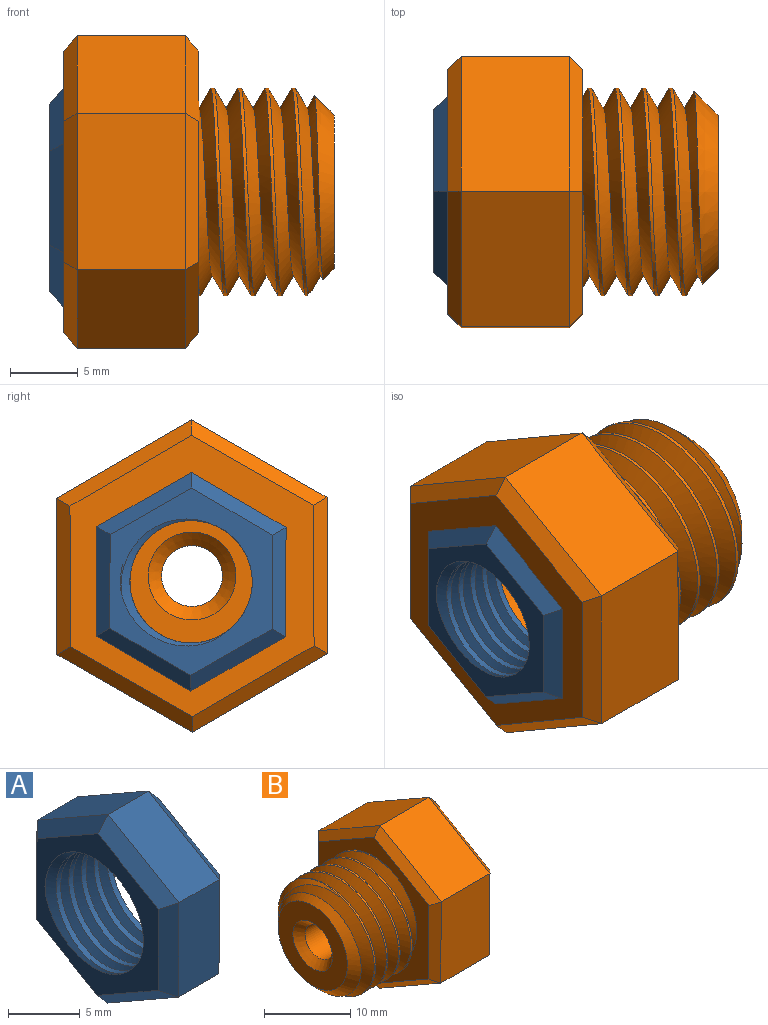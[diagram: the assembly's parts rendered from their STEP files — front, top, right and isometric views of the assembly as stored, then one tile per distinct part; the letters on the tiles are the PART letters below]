
ASSEMBLY  parts=2 mates=1
PART A: 23 faces, bbox 7.5x14.4x16.6 mm
  f0: cylinder r=4.52mm len=9.05mm, axis (1,0,0), area 59.9mm2, adj f7,f8,f21,f22
  f1: plane 6.98x4.07mm, normal (0,-0.5,0.86), area 32.3mm2, adj f2,f6,f14,f18
  f2: plane 8.08x4mm, normal (0,-1,0), area 32.3mm2, adj f1,f3,f12,f16
  f3: plane 7.02x4.01mm, normal (0,-0.5,-0.87), area 32.3mm2, adj f2,f4,f10,f15
  f4: plane 6.98x4.07mm, normal (0,0.5,-0.86), area 32.3mm2, adj f3,f5,f9,f17
  f5: plane 8.08x4mm, normal (0,1,0), area 32.3mm2, adj f4,f6,f11,f19
  f6: plane 7.02x4.01mm, normal (0,0.5,0.87), area 32.3mm2, adj f1,f5,f13,f20
  f7: plane 14.25x12.43mm, normal (-1,0,0), area 53.6mm2, adj f0,f9,f10,f11,f12,f13,f14,f21
  f8: plane 14.27x12.44mm, normal (1,0,0), area 53.6mm2, adj f0,f15,f16,f17,f18,f19,f20,f21
  f9: plane 6.99x4.65mm, normal (-0.71,0.36,-0.61), area 10.6mm2, adj f4,f7,f10,f11
  f10: plane 7.02x4.59mm, normal (-0.71,-0.35,-0.61), area 10.6mm2, adj f3,f7,f9,f12
  f11: plane 8.08x1.03mm, normal (-0.71,0.71,0), area 10.6mm2, adj f5,f7,f9,f13
  f12: plane 8.08x1.03mm, normal (-0.71,-0.71,0), area 10.6mm2, adj f2,f7,f10,f14
  f13: plane 7.02x4.59mm, normal (-0.71,0.35,0.61), area 10.6mm2, adj f6,f7,f11,f14
  f14: plane 6.99x4.65mm, normal (-0.71,-0.36,0.61), area 10.6mm2, adj f1,f7,f12,f13
  f15: plane 7.02x4.59mm, normal (0.71,-0.35,-0.61), area 10.6mm2, adj f3,f8,f16,f17
  f16: plane 8.08x1.03mm, normal (0.71,-0.71,0), area 10.6mm2, adj f2,f8,f15,f18
  f17: plane 6.99x4.65mm, normal (0.71,0.36,-0.61), area 10.6mm2, adj f4,f8,f15,f19
  f18: plane 6.99x4.65mm, normal (0.71,-0.36,0.61), area 10.6mm2, adj f1,f8,f16,f20
  f19: plane 8.08x1.03mm, normal (0.71,0.71,0), area 10.6mm2, adj f5,f8,f17,f20
  f20: plane 7.02x4.59mm, normal (0.71,0.35,0.61), area 10.6mm2, adj f6,f8,f18,f19
  f21: bspline ~12.07x10.45mm, area 119.5mm2, adj f0,f7,f8,f22
  f22: bspline ~12.07x10.45mm, area 119.6mm2, adj f0,f7,f8,f21
PART B: 30 faces, bbox 21.7x21.2x24.2 mm
  f0: cylinder r=7.68mm len=15.36mm, axis (1,0,0), area 50.1mm2, adj f1,f2,f4,f12
  f1: bspline ~17.74x15.36mm, area 332.4mm2, adj f0,f2,f4,f12
  f2: bspline ~17.74x15.36mm, area 332.4mm2, adj f0,f1,f4,f12
  f3: plane 11.36x11.36mm, normal (-1,0,0), area 68.2mm2, adj f4,f28
  f4: cone r=7.68mm half-angle=45deg, axis (1,0,0), area 76.5mm2, adj f0,f1,f2,f3
  f5: plane 9.98x8mm, normal (0,-0.5,0.86), area 92.4mm2, adj f6,f10,f18,f22
  f6: plane 11.55x8mm, normal (0,-1,0), area 92.4mm2, adj f5,f7,f16,f20
  f7: plane 10.02x8mm, normal (0,-0.5,-0.87), area 92.4mm2, adj f6,f8,f14,f19
  f8: plane 9.98x8mm, normal (0,0.5,-0.86), area 92.4mm2, adj f7,f9,f13,f21
  f9: plane 11.55x8mm, normal (0,1,0), area 92.4mm2, adj f8,f10,f15,f23
  f10: plane 10.02x8mm, normal (0,0.5,0.87), area 92.4mm2, adj f5,f9,f17,f24
  f11: plane 20.78x18.04mm, normal (1,0,0), area 167.5mm2, adj f13,f14,f15,f16,f17,f18,f25
  f12: plane 21.9x19.16mm, normal (-1,0,0), area 125.2mm2, adj f0,f1,f2,f19,f20,f21,f22,f23
  f13: plane 9.98x6.38mm, normal (0.71,0.36,-0.61), area 15.5mm2, adj f8,f11,f14,f15
  f14: plane 10.02x6.32mm, normal (0.71,-0.35,-0.61), area 15.5mm2, adj f7,f11,f13,f16
  f15: plane 11.55x1.04mm, normal (0.71,0.71,0), area 15.5mm2, adj f9,f11,f13,f17
  f16: plane 11.55x1.04mm, normal (0.71,-0.71,0), area 15.5mm2, adj f6,f11,f14,f18
  f17: plane 10.02x6.32mm, normal (0.71,0.35,0.61), area 15.5mm2, adj f10,f11,f15,f18
  f18: plane 9.98x6.38mm, normal (0.71,-0.36,0.61), area 15.5mm2, adj f5,f11,f16,f17
  f19: plane 10.02x6.32mm, normal (-0.71,-0.35,-0.61), area 15.5mm2, adj f7,f12,f20,f21
  f20: plane 11.55x1.04mm, normal (-0.71,-0.71,0), area 15.5mm2, adj f6,f12,f19,f22
  f21: plane 9.98x6.38mm, normal (-0.71,0.36,-0.61), area 15.5mm2, adj f8,f12,f19,f23
  f22: plane 9.98x6.38mm, normal (-0.71,-0.36,0.61), area 15.5mm2, adj f5,f12,f20,f24
  f23: plane 11.55x1.04mm, normal (-0.71,0.71,0), area 15.5mm2, adj f9,f12,f21,f24
  f24: plane 10.02x6.32mm, normal (-0.71,0.35,0.61), area 15.5mm2, adj f10,f12,f22,f23
  f25: cylinder r=6mm len=12mm, axis (1,0,0), area 263.9mm2, adj f11,f26
  f26: plane 12x12mm, normal (1,0,0), area 79.9mm2, adj f25,f29
  f27: cylinder r=2.25mm len=11mm, axis (-1,0,0), area 155.5mm2, adj f28,f29
  f28: cone r=2.25mm half-angle=45deg, axis (-1,0,0), area 24.4mm2, adj f3,f27
  f29: cone r=2.25mm half-angle=45deg, axis (1,0,0), area 24.4mm2, adj f26,f27
PLACE A t=(11.8,5.62,3.48)mm
PLACE B rot(axis=(0,1,0),180deg) t=(11.82,5.56,3.91)mm
MATE slider B.f0 <-> A.f8  axis (-1,0,0) through (6.82,5.56,3.91)mm
